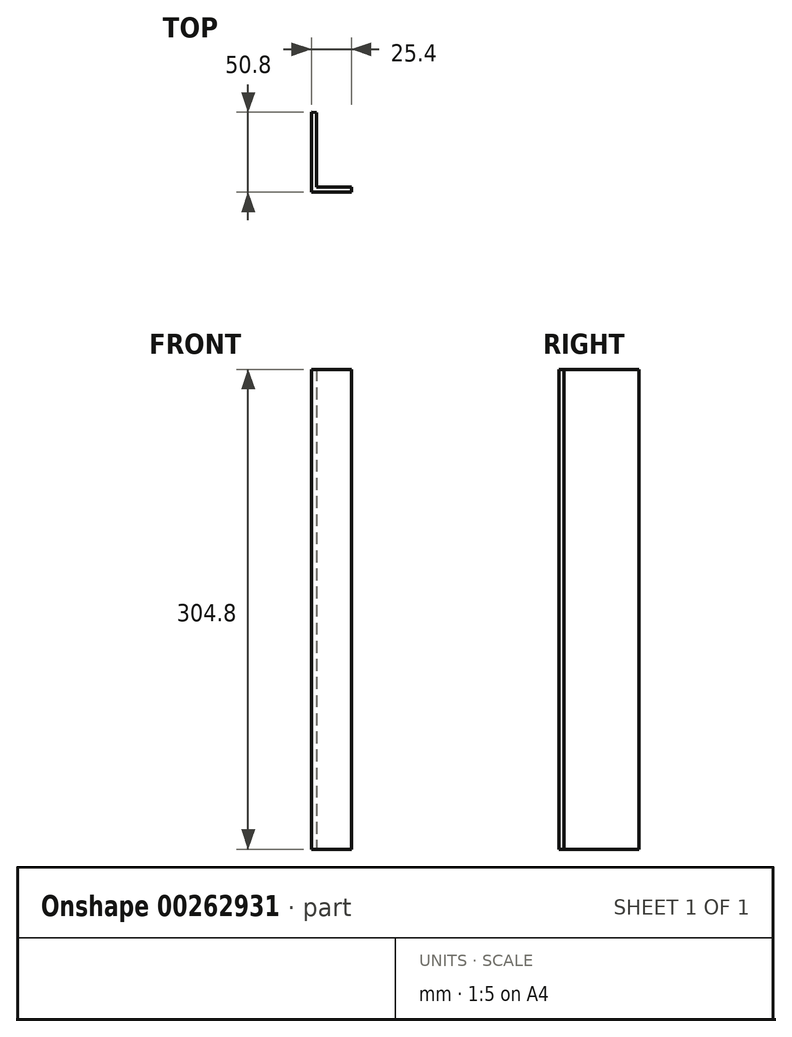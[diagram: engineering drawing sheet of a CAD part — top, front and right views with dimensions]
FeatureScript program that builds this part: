
annotation { "Feature Type Name" : "Feature", "Feature Type Description" : "" }
export const myFeature = defineFeature(function(context is Context, id is Id, definition is map)
    precondition{}
    {
        {
            var Q0;
            Q0=qCreatedBy(makeId("Top.planeOp"),FACE);
            var sketch = newSketch(context, id + "F0", { "sketchPlane" : qUnion([Q0])});
            skLineSegment(sketch, "E0", {"start": v(0, 50.8) * mm, "end": v(0, 0) * mm});
            skLineSegment(sketch, "E1", {"start": v(25.4, 0) * mm, "end": v(25.4, 3.18) * mm});
            skLineSegment(sketch, "E2", {"start": v(25.4, 3.18) * mm, "end": v(3.17, 3.17) * mm});
            skLineSegment(sketch, "E3", {"start": v(3.17, 3.17) * mm, "end": v(3.17, 50.74) * mm});
            skLineSegment(sketch, "E4", {"start": v(3.17, 50.74) * mm, "end": v(0, 50.8) * mm});
            skLineSegment(sketch, "E5", {"start": v(25.4, 0) * mm, "end": v(0, 0) * mm});
            skSolve(sketch);
        }
        {
            var Q0;
            Q0 = qSketchRegion(id + "F0", true);
            extrude(context, id + "F1", {"entities" : qUnion([Q0]), "depth" : 304.8 * mm});
        }
    });
